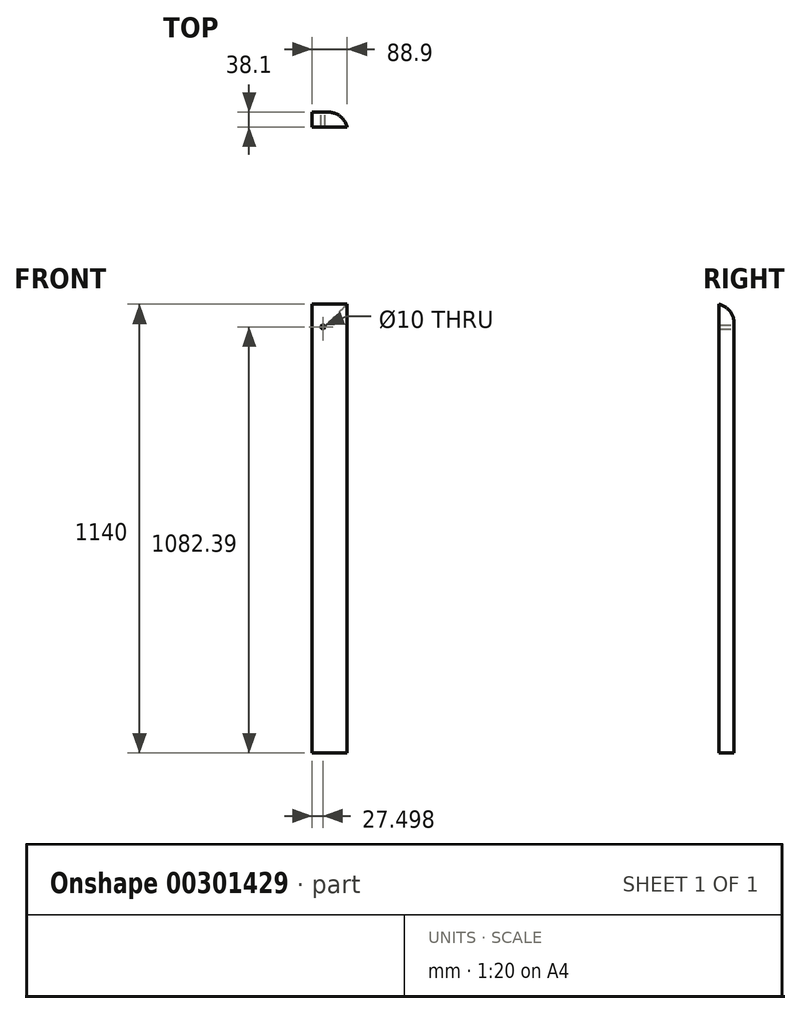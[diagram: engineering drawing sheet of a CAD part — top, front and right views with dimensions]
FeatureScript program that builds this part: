
annotation { "Feature Type Name" : "Feature", "Feature Type Description" : "" }
export const myFeature = defineFeature(function(context is Context, id is Id, definition is map)
    precondition{}
    {
        {
            var Q0;
            Q0=qCreatedBy(makeId("Front.planeOp"),FACE);
            var sketch = newSketch(context, id + "F0", { "sketchPlane" : qUnion([Q0])});
            skLineSegment(sketch, "E0.bottom", {"start": v(-1866.8, -566.32) * mm, "end": v(-1955.7, -566.32) * mm});
            skLineSegment(sketch, "E0.top", {"start": v(-1866.8, 573.68) * mm, "end": v(-1955.7, 573.68) * mm});
            skLineSegment(sketch, "E0.left", {"start": v(-1866.8, -566.32) * mm, "end": v(-1866.8, 573.68) * mm});
            skLineSegment(sketch, "E0.right", {"start": v(-1955.7, -566.32) * mm, "end": v(-1955.7, 573.68) * mm});
            skCircle(sketch, "E1", {"center": v(-1928.2, 516.07) * mm, "radius": 5 * mm});
            skSolve(sketch);
        }
        {
            var Q0;
            Q0=makeQuery(id+"F0.imprint","IMPRINT",FACE,{"disambiguationData":[TD([[makeQuery(id+"F0.imprint","IMPRINT",EDGE,{"derivedFrom":sQuery(id+"F0.wireOp",EDGE,"E0.bottom")}),-1.0]])]});
            extrude(context, id + "F1", {"entities" : qUnion([Q0]), "depth" : 38.1 * mm});
        }
        {
            var Q0;
            Q0=makeQuery(id+"F1.opExtrude","CAP_EDGE",EDGE,{"disambiguationData":[OSD([sQuery(id+"F0.wireOp",EDGE,"E0.left")])],"isStart":true});
            var Q1;
            Q1=makeQuery(id+"F1.opExtrude","CAP_EDGE",EDGE,{"disambiguationData":[OSD([sQuery(id+"F0.wireOp",EDGE,"E0.top")])],"isStart":true});
            fillet(context, id + "F2", {"entities" : qUnion([Q0, Q1]), "radius" : 50 * mm, "tangentPropagation" : true, "allowEdgeOverflow" : false});
        }
    });
